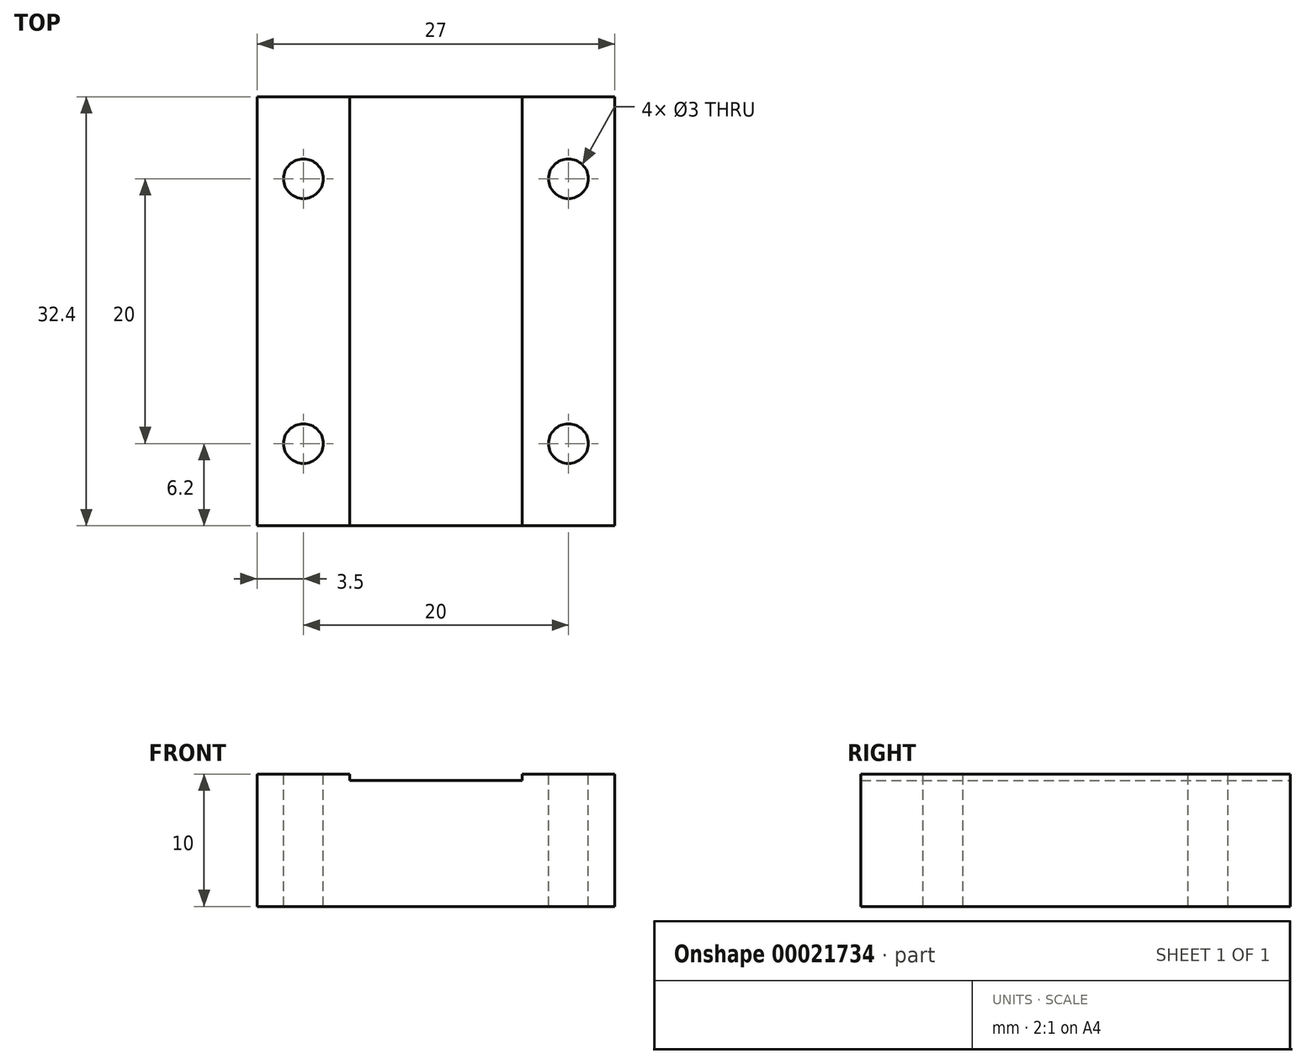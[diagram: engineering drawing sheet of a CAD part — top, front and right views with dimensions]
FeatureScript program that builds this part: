
annotation { "Feature Type Name" : "Feature", "Feature Type Description" : "" }
export const myFeature = defineFeature(function(context is Context, id is Id, definition is map)
    precondition{}
    {
        {
            var Q0;
            Q0=qCreatedBy(makeId("Front.planeOp"),FACE);
            var sketch = newSketch(context, id + "F0", { "sketchPlane" : qUnion([Q0])});
            skLineSegment(sketch, "E0", {"start": v(-13.5, 0) * mm, "end": v(-6.5, 0) * mm});
            skLineSegment(sketch, "E1", {"start": v(-6.5, 0) * mm, "end": v(-6.5, -0.5) * mm});
            skLineSegment(sketch, "E2", {"start": v(-6.5, -0.5) * mm, "end": v(6.5, -0.5) * mm});
            skLineSegment(sketch, "E3", {"start": v(6.5, -0.5) * mm, "end": v(6.5, 0) * mm});
            skLineSegment(sketch, "E4", {"start": v(6.5, 0) * mm, "end": v(13.5, 0) * mm});
            skLineSegment(sketch, "E5", {"start": v(13.5, 0) * mm, "end": v(13.5, -10) * mm});
            skLineSegment(sketch, "E6", {"start": v(13.5, -10) * mm, "end": v(-13.5, -10) * mm});
            skLineSegment(sketch, "E7", {"start": v(-13.5, -10) * mm, "end": v(-13.5, 0) * mm});
            skSolve(sketch);
        }
        {
            var Q0;
            Q0=makeQuery(id+"F0.imprint","IMPRINT",FACE,{"disambiguationData":[TD([[makeQuery(id+"F0.imprint","IMPRINT",EDGE,{"derivedFrom":sQuery(id+"F0.wireOp",EDGE,"E0")}),-1.0]])]});
            extrude(context, id + "F1", {"entities" : qUnion([Q0]), "depth" : 16.2 * mm});
        }
        {
            var Q0;
            Q0=makeQuery(id+"F1.opExtrude","SWEPT_FACE",FACE,{"disambiguationData":[OSD([sQuery(id+"F0.wireOp",EDGE,"E0")])]});
            var sketch = newSketch(context, id + "F2", { "sketchPlane" : qUnion([Q0])});
            skCircle(sketch, "E8", {"center": v(-10, -10) * mm, "radius": 1.5 * mm});
            skCircle(sketch, "E9", {"center": v(10, -10) * mm, "radius": 1.5 * mm});
            skSolve(sketch);
        }
        {
            var Q0;
            Q0=makeQuery(id+"F2.imprint","IMPRINT",FACE,{"disambiguationData":[TD([[makeQuery(id+"F2.imprint","IMPRINT",EDGE,{"derivedFrom":sQuery(id+"F2.wireOp",EDGE,"E8")}),1.0]])]});
            var Q1;
            Q1=makeQuery(id+"F2.imprint","IMPRINT",FACE,{"disambiguationData":[TD([[makeQuery(id+"F2.imprint","IMPRINT",EDGE,{"derivedFrom":sQuery(id+"F2.wireOp",EDGE,"E9")}),1.0]])]});
            extrude(context, id + "F3", {"entities" : qUnion([Q0, Q1]), "operationType" : NewBodyOperationType.REMOVE, "oppositeDirection" : true, "depth" : 10.5 * mm});
        }
        {
            var Q0;
            Q0=makeQuery(id+"F1.opExtrude","SWEPT_BODY",BODY,{"disambiguationData":[OSD([sQuery(id+"F0.wireOp",EDGE,"E0"),sQuery(id+"F0.wireOp",EDGE,"E1"),sQuery(id+"F0.wireOp",EDGE,"E2"),sQuery(id+"F0.wireOp",EDGE,"E3"),sQuery(id+"F0.wireOp",EDGE,"E4"),sQuery(id+"F0.wireOp",EDGE,"E5"),sQuery(id+"F0.wireOp",EDGE,"E6"),sQuery(id+"F0.wireOp",EDGE,"E7")])]});
            var Q1;
            Q1=makeQuery(id+"F1.opExtrude","CAP_FACE",FACE,{"disambiguationData":[OSD([sQuery(id+"F0.wireOp",EDGE,"E0"),sQuery(id+"F0.wireOp",EDGE,"E1"),sQuery(id+"F0.wireOp",EDGE,"E2"),sQuery(id+"F0.wireOp",EDGE,"E3"),sQuery(id+"F0.wireOp",EDGE,"E4"),sQuery(id+"F0.wireOp",EDGE,"E5"),sQuery(id+"F0.wireOp",EDGE,"E6"),sQuery(id+"F0.wireOp",EDGE,"E7")])],"isStart":true});
            mirror(context, id + "F4", {"operationType" : NewBodyOperationType.ADD, "entities" : qUnion([Q0]), "mirrorPlane" : qUnion([Q1])});
        }
    });
